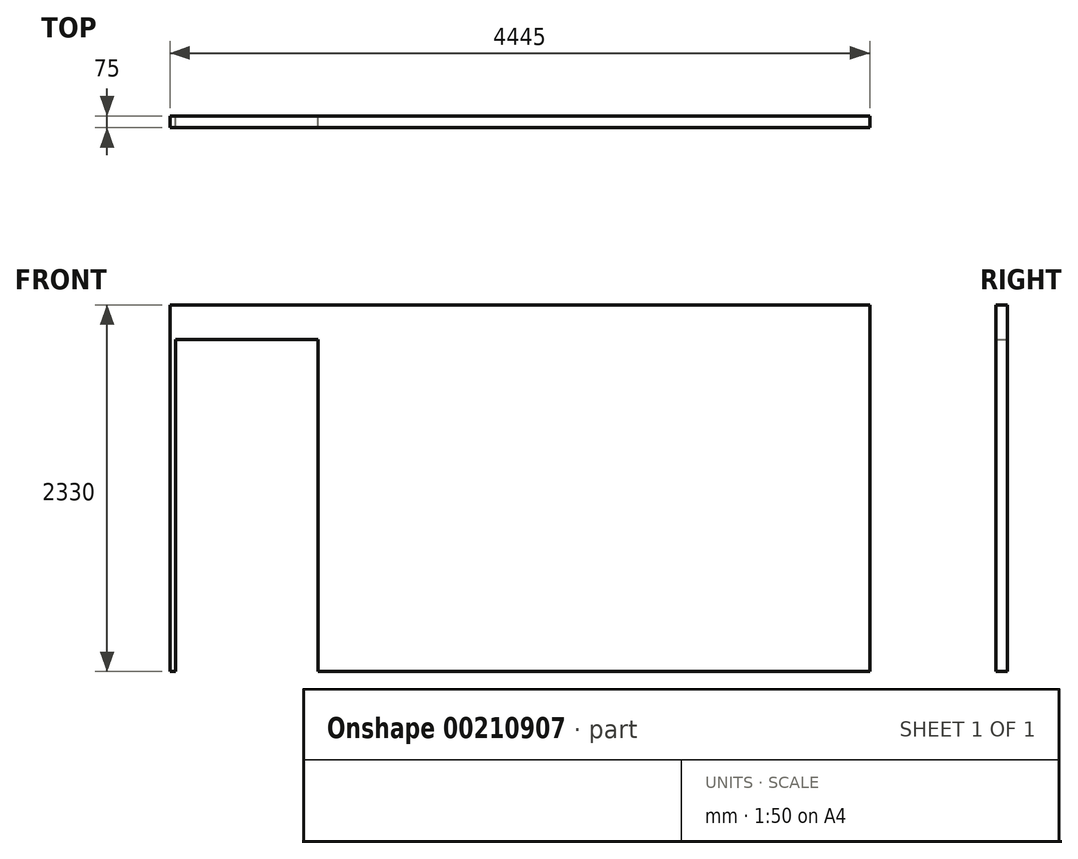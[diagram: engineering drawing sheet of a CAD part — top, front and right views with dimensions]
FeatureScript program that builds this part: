
annotation { "Feature Type Name" : "Feature", "Feature Type Description" : "" }
export const myFeature = defineFeature(function(context is Context, id is Id, definition is map)
    precondition{}
    {
        {
            var Q0;
            Q0=qCreatedBy(makeId("Front.planeOp"),FACE);
            var sketch = newSketch(context, id + "F0", { "sketchPlane" : qUnion([Q0])});
            skLineSegment(sketch, "E0.bottom", {"start": v(0, 0) * mm, "end": v(4445, 0) * mm});
            skLineSegment(sketch, "E0.right", {"start": v(4445, 0) * mm, "end": v(4445, 2330) * mm});
            skLineSegment(sketch, "E1", {"start": v(0, 0) * mm, "end": v(0, 2330) * mm});
            skLineSegment(sketch, "E2", {"start": v(0, 2330) * mm, "end": v(4445, 2330) * mm});
            skLineSegment(sketch, "E3.bottom", {"start": v(35, 0) * mm, "end": v(940, 0) * mm});
            skLineSegment(sketch, "E3.top", {"start": v(35, 2110) * mm, "end": v(940, 2110) * mm});
            skLineSegment(sketch, "E3.left", {"start": v(35, 0) * mm, "end": v(35, 2110) * mm});
            skLineSegment(sketch, "E3.right", {"start": v(940, 0) * mm, "end": v(940, 2110) * mm});
            skSolve(sketch);
        }
        {
            var Q0;
            Q0=makeQuery(id+"F0.imprint","IMPRINT",FACE,{"disambiguationData":[TD([[makeQuery(id+"F0.imprint","IMPRINT",EDGE,{"derivedFrom":sQuery(id+"F0.wireOp",EDGE,"E0.bottom")}),1.0]])]});
            extrude(context, id + "F1", {"entities" : qUnion([Q0]), "depth" : 75 * mm});
        }
    });
